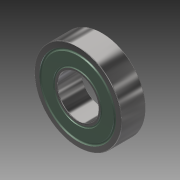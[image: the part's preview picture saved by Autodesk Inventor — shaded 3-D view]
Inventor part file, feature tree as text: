
AUTODESK INVENTOR PART (.ipt)
format: ipt  version: 2014 (Build 180170000, 170)  size: 180,736 bytes
history: native  units: in
note: dims shown in document units (in); Inventor stores cm internally (conversion verified against a paired STEP export)
features: sketch x2, extrude x1, fillet x1, revolve x1, plane x1, mirror x1
ambient origin geometry x8: Origin, YZ Plane, XZ Plane, XY Plane, X Axis, Y Axis, Z Axis, Center Point
bodies: Solid1 (feature_tree)
feature tree (7):
  extrude  "Extrusion1"  Depth=0.3543in
  fillet  "Fillet1"  Radius=0.3543in
  revolve  "Revolution1"  Angle=90.0deg
  plane  "Work Plane1"
  mirror  "Mirror1"
  sketch  "Sketch1"  dims[d0=0.5906in d1=1.2598in d2=0.3543in d3=0.0in]
  sketch  "Sketch2"  dims[d4=0.0118in d5=90.0deg]
